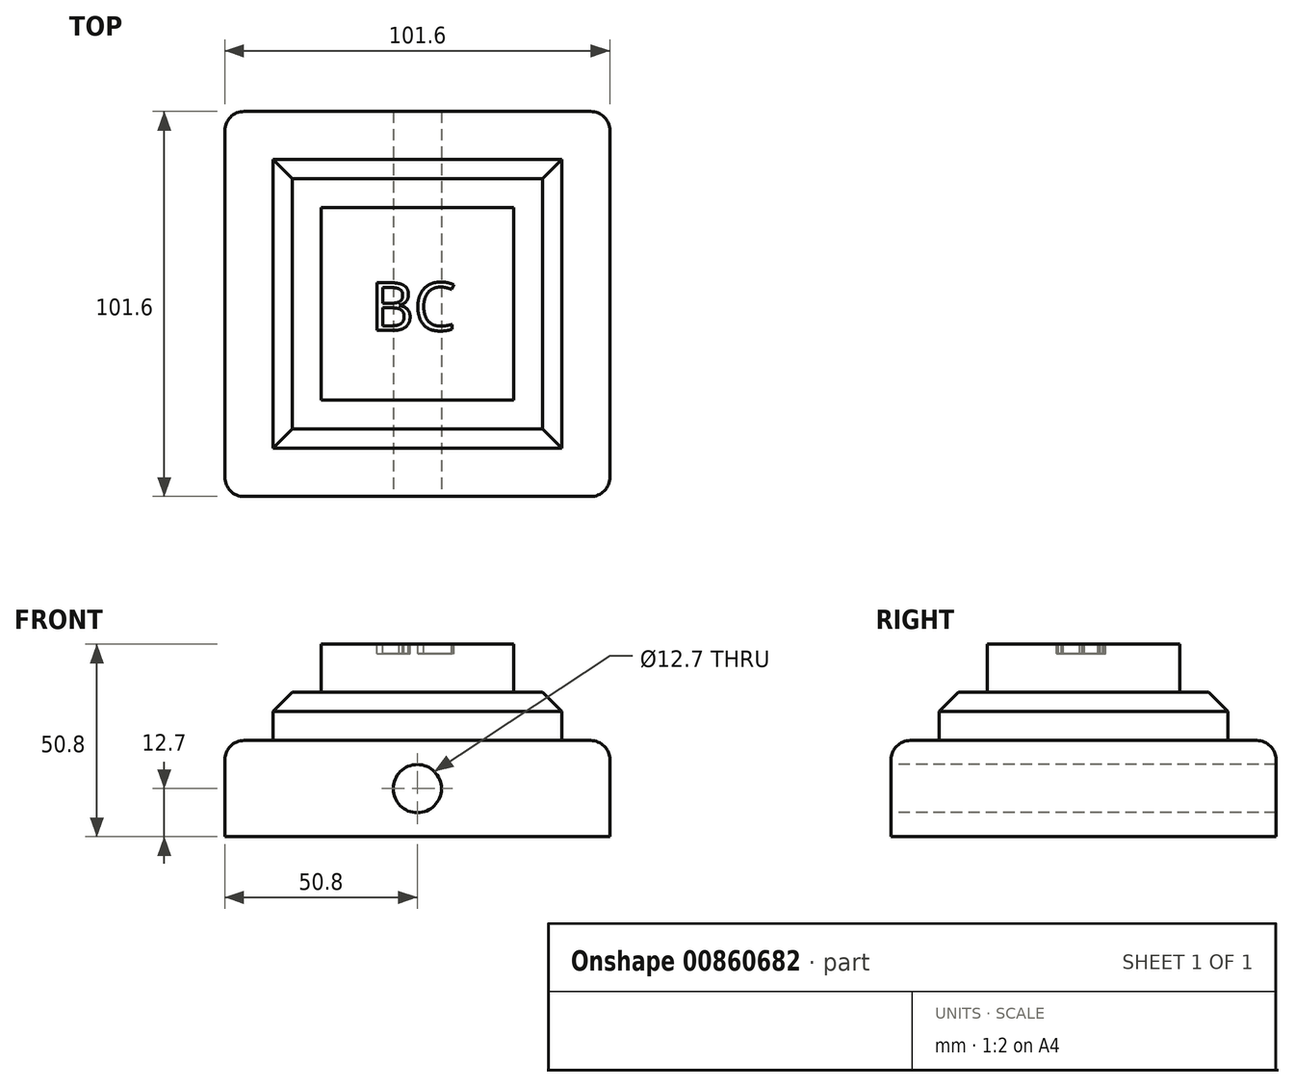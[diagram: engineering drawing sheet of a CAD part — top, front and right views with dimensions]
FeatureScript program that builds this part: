
annotation { "Feature Type Name" : "Feature", "Feature Type Description" : "" }
export const myFeature = defineFeature(function(context is Context, id is Id, definition is map)
    precondition{}
    {
        {
            var Q0;
            Q0=qCreatedBy(makeId("Top.planeOp"),FACE);
            var sketch = newSketch(context, id + "F0", { "sketchPlane" : qUnion([Q0])});
            skLineSegment(sketch, "E0.bottom", {"start": v(0, 0) * mm, "end": v(101.6, 0) * mm});
            skLineSegment(sketch, "E0.top", {"start": v(0, 101.6) * mm, "end": v(101.6, 101.6) * mm});
            skLineSegment(sketch, "E0.left", {"start": v(0, 0) * mm, "end": v(0, 101.6) * mm});
            skLineSegment(sketch, "E0.right", {"start": v(101.6, 0) * mm, "end": v(101.6, 101.6) * mm});
            skSolve(sketch);
        }
        {
            var Q0;
            Q0 = qSketchRegion(id + "F0", true);
            extrude(context, id + "F1", {"entities" : qUnion([Q0]), "depth" : 25.4 * mm, "offsetDistance" : 25.4 * mm});
        }
        {
            var Q0;
            Q0=makeQuery(id+"F1.opExtrude","CAP_FACE",FACE,{"disambiguationData":[OSD([sQuery(id+"F0.wireOp",EDGE,"E0.bottom"),sQuery(id+"F0.wireOp",EDGE,"E0.top"),sQuery(id+"F0.wireOp",EDGE,"E0.left"),sQuery(id+"F0.wireOp",EDGE,"E0.right")])],"isStart":false});
            var sketch = newSketch(context, id + "F2", { "sketchPlane" : qUnion([Q0])});
            skLineSegment(sketch, "E1.bottom", {"start": v(12.7, 12.7) * mm, "end": v(88.9, 12.7) * mm});
            skLineSegment(sketch, "E1.top", {"start": v(12.7, 88.9) * mm, "end": v(88.9, 88.9) * mm});
            skLineSegment(sketch, "E1.left", {"start": v(12.7, 12.7) * mm, "end": v(12.7, 88.9) * mm});
            skLineSegment(sketch, "E1.right", {"start": v(88.9, 12.7) * mm, "end": v(88.9, 88.9) * mm});
            skSolve(sketch);
        }
        {
            var Q0;
            Q0=makeQuery(id+"F2.imprint","IMPRINT",FACE,{"disambiguationData":[TD([[makeQuery(id+"F2.imprint","IMPRINT",EDGE,{"derivedFrom":sQuery(id+"F2.wireOp",EDGE,"E1.bottom")}),1.0]])]});
            extrude(context, id + "F3", {"entities" : qUnion([Q0]), "operationType" : NewBodyOperationType.ADD, "depth" : 12.7 * mm, "offsetDistance" : 25.4 * mm});
        }
        {
            var Q0;
            Q0=makeQuery(id+"F3.opExtrude","CAP_FACE",FACE,{"disambiguationData":[OSD([sQuery(id+"F2.wireOp",EDGE,"E1.bottom"),sQuery(id+"F2.wireOp",EDGE,"E1.top"),sQuery(id+"F2.wireOp",EDGE,"E1.left"),sQuery(id+"F2.wireOp",EDGE,"E1.right")])],"isStart":false});
            var sketch = newSketch(context, id + "F4", { "sketchPlane" : qUnion([Q0])});
            skLineSegment(sketch, "E2.bottom", {"start": v(25.4, 25.4) * mm, "end": v(76.2, 25.4) * mm});
            skLineSegment(sketch, "E2.top", {"start": v(25.4, 76.2) * mm, "end": v(76.2, 76.2) * mm});
            skLineSegment(sketch, "E2.left", {"start": v(25.4, 25.4) * mm, "end": v(25.4, 76.2) * mm});
            skLineSegment(sketch, "E2.right", {"start": v(76.2, 25.4) * mm, "end": v(76.2, 76.2) * mm});
            skSolve(sketch);
        }
        {
            var Q0;
            Q0=makeQuery(id+"F4.imprint","IMPRINT",FACE,{"disambiguationData":[TD([[makeQuery(id+"F4.imprint","IMPRINT",EDGE,{"derivedFrom":sQuery(id+"F4.wireOp",EDGE,"E2.bottom")}),1.0]])]});
            extrude(context, id + "F5", {"entities" : qUnion([Q0]), "operationType" : NewBodyOperationType.ADD, "depth" : 12.7 * mm, "offsetDistance" : 25.4 * mm});
        }
        {
            var Q0;
            Q0=makeQuery(id+"F1.opExtrude","SWEPT_FACE",FACE,{"disambiguationData":[OSD([sQuery(id+"F0.wireOp",EDGE,"E0.bottom")])]});
            var sketch = newSketch(context, id + "F6", { "sketchPlane" : qUnion([Q0])});
            skCircle(sketch, "E3", {"center": v(50.8, 12.7) * mm, "radius": 6.35 * mm});
            skSolve(sketch);
        }
        {
            var Q0;
            Q0=makeQuery(id+"F6.imprint","IMPRINT",FACE,{"disambiguationData":[TD([[makeQuery(id+"F6.imprint","IMPRINT",EDGE,{"derivedFrom":sQuery(id+"F6.wireOp",EDGE,"E3")}),1.0]])]});
            extrude(context, id + "F7", {"entities" : qUnion([Q0]), "operationType" : NewBodyOperationType.REMOVE, "oppositeDirection" : true, "depth" : 127 * mm, "offsetDistance" : 25.4 * mm});
        }
        {
            var Q0;
            Q0=makeQuery(id+"F1.opExtrude","CAP_EDGE",EDGE,{"disambiguationData":[OSD([sQuery(id+"F0.wireOp",EDGE,"E0.bottom")])],"isStart":false});
            fillet(context, id + "F8", {"entities" : qUnion([Q0]), "radius" : 5.08 * mm, "tangentPropagation" : true, "allowEdgeOverflow" : false});
        }
        {
            var Q0;
            Q0=makeQuery(id+"F1.opExtrude","CAP_EDGE",EDGE,{"disambiguationData":[OSD([sQuery(id+"F0.wireOp",EDGE,"E0.left")])],"isStart":false});
            fillet(context, id + "F9", {"entities" : qUnion([Q0]), "radius" : 5.08 * mm, "tangentPropagation" : true, "allowEdgeOverflow" : false});
        }
        {
            var Q0;
            Q0=makeQuery(id+"F1.opExtrude","CAP_EDGE",EDGE,{"disambiguationData":[OSD([sQuery(id+"F0.wireOp",EDGE,"E0.top")])],"isStart":false});
            fillet(context, id + "F10", {"entities" : qUnion([Q0]), "radius" : 5.08 * mm, "tangentPropagation" : true, "allowEdgeOverflow" : false});
        }
        {
            var Q0;
            Q0=makeQuery(id+"F1.opExtrude","CAP_EDGE",EDGE,{"disambiguationData":[OSD([sQuery(id+"F0.wireOp",EDGE,"E0.right")])],"isStart":false});
            fillet(context, id + "F11", {"entities" : qUnion([Q0]), "radius" : 5.08 * mm, "tangentPropagation" : true, "allowEdgeOverflow" : false});
        }
        {
            var Q0;
            Q0=makeQuery(id+"F3.opExtrude","CAP_EDGE",EDGE,{"disambiguationData":[OSD([sQuery(id+"F2.wireOp",EDGE,"E1.right")])],"isStart":false});
            chamfer(context, id + "F12", {"entities" : qUnion([Q0]), "width" : 5.08 * mm, "tangentPropagation" : true});
        }
        {
            var Q0;
            Q0=makeQuery(id+"F3.opExtrude","CAP_EDGE",EDGE,{"disambiguationData":[OSD([sQuery(id+"F2.wireOp",EDGE,"E1.top")])],"isStart":false});
            chamfer(context, id + "F13", {"entities" : qUnion([Q0]), "width" : 5.08 * mm, "tangentPropagation" : true});
        }
        {
            var Q0;
            Q0=makeQuery(id+"F3.opExtrude","CAP_EDGE",EDGE,{"disambiguationData":[OSD([sQuery(id+"F2.wireOp",EDGE,"E1.left")])],"isStart":false});
            chamfer(context, id + "F14", {"entities" : qUnion([Q0]), "width" : 5.08 * mm, "tangentPropagation" : true});
        }
        {
            var Q0;
            Q0=makeQuery(id+"F3.opExtrude","CAP_EDGE",EDGE,{"disambiguationData":[OSD([sQuery(id+"F2.wireOp",EDGE,"E1.bottom")])],"isStart":false});
            chamfer(context, id + "F15", {"entities" : qUnion([Q0]), "width" : 5.08 * mm, "tangentPropagation" : true});
        }
        {
            var Q0;
            Q0=makeQuery(id+"F5.opExtrude","CAP_FACE",FACE,{"disambiguationData":[OSD([sQuery(id+"F4.wireOp",EDGE,"E2.bottom"),sQuery(id+"F4.wireOp",EDGE,"E2.top"),sQuery(id+"F4.wireOp",EDGE,"E2.left"),sQuery(id+"F4.wireOp",EDGE,"E2.right")])],"isStart":false});
            var sketch = newSketch(context, id + "F16", { "sketchPlane" : qUnion([Q0])});
            skText(sketch, "E4", { "text": "BC", "fontName": "OpenSans-Regular.ttf"});
            const initialGuessF16  = {"E4": [0.03843, 0.04382, 1, 0, 0.0127]};
            skSetInitialGuess(sketch, initialGuessF16);
            skSolve(sketch);
        }
        {
            var Q0;
            Q0 = qSketchRegion(id + "F16", true);
            extrude(context, id + "F17", {"entities" : qUnion([Q0]), "operationType" : NewBodyOperationType.REMOVE, "oppositeDirection" : true, "depth" : 2.54 * mm, "offsetDistance" : 25.4 * mm});
        }
    });
